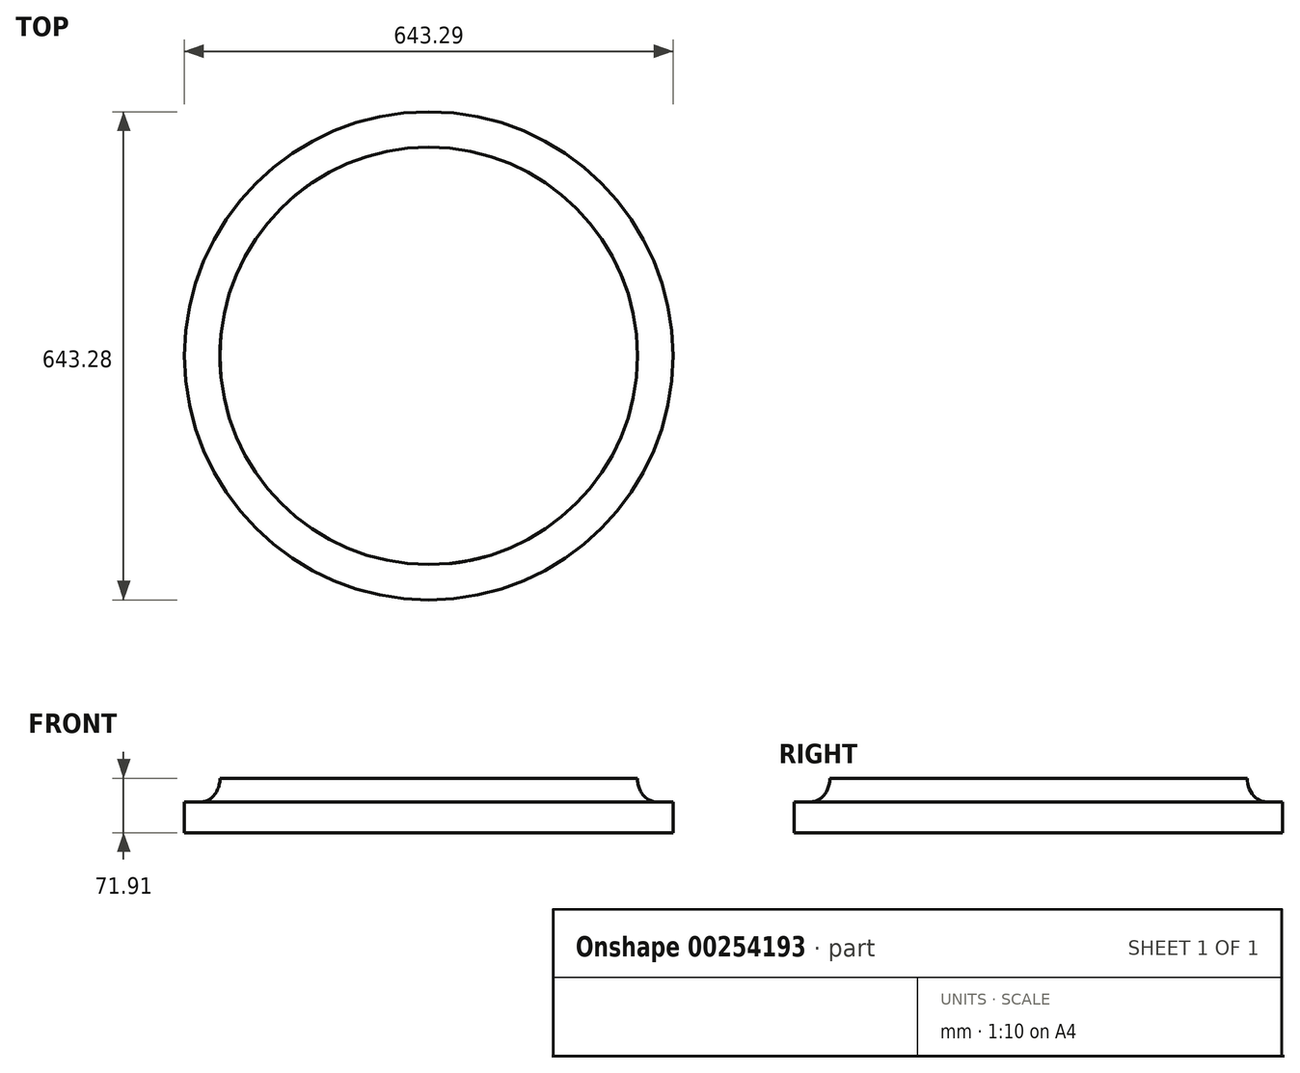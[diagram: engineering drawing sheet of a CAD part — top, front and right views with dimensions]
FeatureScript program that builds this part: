
annotation { "Feature Type Name" : "Feature", "Feature Type Description" : "" }
export const myFeature = defineFeature(function(context is Context, id is Id, definition is map)
    precondition{}
    {
        {
            var Q0;
            Q0=qCreatedBy(makeId("Front.planeOp"),FACE);
            var sketch = newSketch(context, id + "F0", { "sketchPlane" : qUnion([Q0])});
            skLineSegment(sketch, "E0", {"start": v(-270.96, 0) * mm, "end": v(4.04, 0) * mm});
            skLineSegment(sketch, "E1", {"start": v(4.04, 0) * mm, "end": v(4.04, -31) * mm, "construction": true});
            skLineSegment(sketch, "E2", {"start": v(4.04, -31) * mm, "end": v(29.04, -31) * mm, "construction": true});
            skEllipticalArc(sketch, "E3", {});
            skLineSegment(sketch, "E4", {"start": v(29.04, -31) * mm, "end": v(50.69, -31) * mm});
            skLineSegment(sketch, "E5", {"start": v(50.69, -31) * mm, "end": v(50.69, -71.91) * mm});
            skLineSegment(sketch, "E6", {"start": v(50.69, -71.91) * mm, "end": v(-270.96, -71.91) * mm});
            skLineSegment(sketch, "E7", {"start": v(-270.96, -71.91) * mm, "end": v(-270.96, 0) * mm});
            const initialGuessF0  = {"E3": [0.029044104784316793, 0, 0, -1, 0.031, 0.025, 4.71238898038469, 0]};
            skSetInitialGuess(sketch, initialGuessF0);
            skSolve(sketch);
        }
        {
            var Q0;
            Q0 = qSketchRegion(id + "F0", true);
            var Q1;
            Q1=sQuery(id+"F0.wireOp",EDGE,"E7");
            revolve(context, id + "F1", {"entities" : qUnion([Q0]), "axis" : qUnion([Q1]), "revolveType" : RevolveType.FULL});
        }
    });
